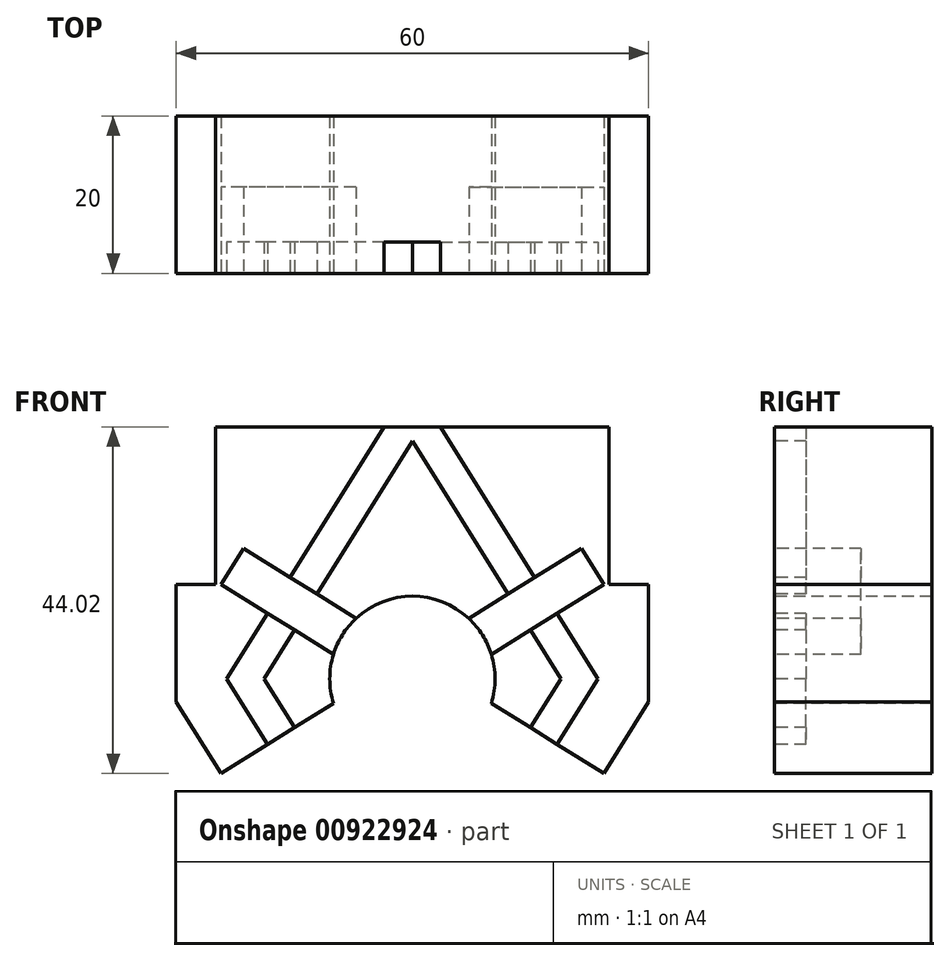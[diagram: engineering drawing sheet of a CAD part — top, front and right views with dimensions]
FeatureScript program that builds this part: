
annotation { "Feature Type Name" : "Feature", "Feature Type Description" : "" }
export const myFeature = defineFeature(function(context is Context, id is Id, definition is map)
    precondition{}
    {
        {
            var Q0;
            Q0=qCreatedBy(makeId("Front.planeOp"),FACE);
            var sketch = newSketch(context, id + "F0", { "sketchPlane" : qUnion([Q0])});
            skLineSegment(sketch, "E0", {"start": v(-28.13, -17.58) * mm, "end": v(31.4, 19.63) * mm, "construction": true});
            skLineSegment(sketch, "E1", {"start": v(7.3, 22.28) * mm, "end": v(22.97, -2.8) * mm, "construction": true});
            skArc(sketch, "E2", {"start": v(10.04, -3.09) * mm, "mid": v(0, 10.5) * mm, "end": v(-10.04, -3.09) * mm});
            skLineSegment(sketch, "E3", {"start": v(0, -23.09) * mm, "end": v(0, 36.36) * mm, "construction": true});
            skLineSegment(sketch, "E4", {"start": v(-33.15, 0) * mm, "end": v(34.43, 0) * mm, "construction": true});
            skLineSegment(sketch, "E5", {"start": v(0, 32) * mm, "end": v(25, 32) * mm});
            skLineSegment(sketch, "E6", {"start": v(25, 32) * mm, "end": v(25, 12) * mm});
            skLineSegment(sketch, "E7", {"start": v(25, 12) * mm, "end": v(30, 12) * mm});
            skLineSegment(sketch, "E8", {"start": v(30, 12) * mm, "end": v(30, -2.94) * mm});
            skLineSegment(sketch, "E9", {"start": v(30, -2.94) * mm, "end": v(24.33, -12.02) * mm});
            skLineSegment(sketch, "E10.MirrorCS", {"start": v(0, 32) * mm, "end": v(-25, 32) * mm});
            skLineSegment(sketch, "E11.MirrorCS", {"start": v(-25, 32) * mm, "end": v(-25, 12) * mm});
            skLineSegment(sketch, "E12.MirrorCS", {"start": v(-25, 12) * mm, "end": v(-30, 12) * mm});
            skLineSegment(sketch, "E13.MirrorCS", {"start": v(-30, 12) * mm, "end": v(-30, -2.94) * mm});
            skLineSegment(sketch, "E14.MirrorCS", {"start": v(-30, -2.94) * mm, "end": v(-24.33, -12.02) * mm});
            skLineSegment(sketch, "E15", {"start": v(7.17, 7.67) * mm, "end": v(21.47, 16.6) * mm});
            skLineSegment(sketch, "E16.MirrorCS", {"start": v(10.04, 3.09) * mm, "end": v(24.33, 12.02) * mm});
            skLineSegment(sketch, "E17", {"start": v(21.47, 16.6) * mm, "end": v(24.33, 12.02) * mm});
            skLineSegment(sketch, "E18", {"start": v(0, 30.2) * mm, "end": v(18.87, 0) * mm});
            skLineSegment(sketch, "E19", {"start": v(3.59, 32) * mm, "end": v(23.58, 0) * mm});
            skLineSegment(sketch, "E20.MirrorCS", {"start": v(0, 30.2) * mm, "end": v(-18.87, 0) * mm});
            skLineSegment(sketch, "E21.MirrorCS", {"start": v(-3.59, 32) * mm, "end": v(-23.58, 0) * mm});
            skLineSegment(sketch, "E22.MirrorCS", {"start": v(-7.17, 7.67) * mm, "end": v(-21.47, 16.6) * mm});
            skLineSegment(sketch, "E23.MirrorCS", {"start": v(-10.04, 3.09) * mm, "end": v(-24.33, 12.02) * mm});
            skLineSegment(sketch, "E24.MirrorCS", {"start": v(-21.47, 16.6) * mm, "end": v(-24.33, 12.02) * mm});
            skLineSegment(sketch, "E25.MirrorCS", {"start": v(-15, -6.19) * mm, "end": v(-18.87, 0) * mm});
            skLineSegment(sketch, "E26.MirrorCS", {"start": v(-18.4, -8.3) * mm, "end": v(-23.58, 0) * mm});
            skLineSegment(sketch, "E27.MirrorCS", {"start": v(18.4, -8.3) * mm, "end": v(23.58, 0) * mm});
            skLineSegment(sketch, "E28.MirrorCS", {"start": v(15, -6.19) * mm, "end": v(18.87, 0) * mm});
            skLineSegment(sketch, "E29.MirrorCS", {"start": v(10.04, -3.09) * mm, "end": v(24.33, -12.02) * mm});
            skLineSegment(sketch, "E30.MirrorCS", {"start": v(-10.04, -3.09) * mm, "end": v(-24.33, -12.02) * mm});
            skSolve(sketch);
        }
        {
            var Q0;
            Q0=qSketchRegion(id+"F0",true);
            var Q1;
            {var subQ1=sQuery(id+"F0.wireOp",EDGE,"E18");var subQ8=sQuery(id+"F0.wireOp",EDGE,"E15");var subQ10=makeQuery(id+"F0.imprint","INTERSECT",VERTEX,{"derivedFrom":[subQ8,subQ1]});Q1=makeQuery(id+"F0.imprint","IMPRINT",FACE,{"disambiguationData":[TD([[makeQuery(id+"F0.imprint","IMPRINT",EDGE,{"disambiguationData":[TD([[subQ10,-1.0]])],"derivedFrom":subQ8}),1.0]])]});}
            var Q2;
            {var subQ0=sQuery(id+"F0.wireOp",EDGE,"E17");Q2=makeQuery(id+"F0.imprint","IMPRINT",FACE,{"disambiguationData":[TD([[makeQuery(id+"F0.imprint","IMPRINT",EDGE,{"derivedFrom":subQ0}),-1.0]])]});}
            var Q3;
            {var subQ0=sQuery(id+"F0.wireOp",EDGE,"E18");var subQ1=sQuery(id+"F0.wireOp",EDGE,"E15");var subQ2=makeQuery(id+"F0.imprint","INTERSECT",VERTEX,{"derivedFrom":[subQ1,subQ0]});Q3=makeQuery(id+"F0.imprint","IMPRINT",FACE,{"disambiguationData":[TD([[makeQuery(id+"F0.imprint","IMPRINT",EDGE,{"disambiguationData":[TD([[subQ2,-1.0]])],"derivedFrom":subQ1}),-1.0]])]});}
            var Q4;
            {var subQ0=sQuery(id+"F0.wireOp",EDGE,"E22.MirrorCS");var subQ1=sQuery(id+"F0.wireOp",EDGE,"E20.MirrorCS");var subQ2=makeQuery(id+"F0.imprint","INTERSECT",VERTEX,{"derivedFrom":[subQ1,subQ0]});Q4=makeQuery(id+"F0.imprint","IMPRINT",FACE,{"disambiguationData":[TD([[makeQuery(id+"F0.imprint","IMPRINT",EDGE,{"disambiguationData":[TD([[subQ2,-1.0]])],"derivedFrom":subQ1}),-1.0]])]});}
            var Q5;
            {var subQ5=sQuery(id+"F0.wireOp",EDGE,"E24.MirrorCS");Q5=makeQuery(id+"F0.imprint","IMPRINT",FACE,{"disambiguationData":[TD([[makeQuery(id+"F0.imprint","IMPRINT",EDGE,{"derivedFrom":subQ5}),1.0]])]});}
            extrude(context, id + "F1", {"entities" : qUnion([Q0, Q1, Q2, Q3, Q4, Q5]), "oppositeDirection" : true, "depth" : 20 * mm, "offsetDistance" : 25 * mm});
        }
        {
            var Q0;
            {var subQ0=sQuery(id+"F0.wireOp",EDGE,"E17");Q0=makeQuery(id+"F0.imprint","IMPRINT",FACE,{"disambiguationData":[TD([[makeQuery(id+"F0.imprint","IMPRINT",EDGE,{"derivedFrom":subQ0}),-1.0]])]});}
            var Q1;
            {var subQ0=sQuery(id+"F0.wireOp",EDGE,"E18");var subQ1=sQuery(id+"F0.wireOp",EDGE,"E15");var subQ2=makeQuery(id+"F0.imprint","INTERSECT",VERTEX,{"derivedFrom":[subQ1,subQ0]});Q1=makeQuery(id+"F0.imprint","IMPRINT",FACE,{"disambiguationData":[TD([[makeQuery(id+"F0.imprint","IMPRINT",EDGE,{"disambiguationData":[TD([[subQ2,-1.0]])],"derivedFrom":subQ1}),-1.0]])]});}
            var Q2;
            {var subQ0=sQuery(id+"F0.wireOp",EDGE,"E15");var subQ1=sQuery(id+"F0.wireOp",EDGE,"E2");var subQ2=makeQuery(id+"F0.imprint","INTERSECT",VERTEX,{"derivedFrom":[subQ1,subQ0]});Q2=makeQuery(id+"F0.imprint","IMPRINT",FACE,{"disambiguationData":[TD([[makeQuery(id+"F0.imprint","IMPRINT",EDGE,{"disambiguationData":[TD([[subQ2,1.0]])],"derivedFrom":subQ1}),-1.0]])]});}
            var Q3;
            {var subQ0=sQuery(id+"F0.wireOp",EDGE,"E22.MirrorCS");var subQ1=sQuery(id+"F0.wireOp",EDGE,"E20.MirrorCS");var subQ2=makeQuery(id+"F0.imprint","INTERSECT",VERTEX,{"derivedFrom":[subQ1,subQ0]});Q3=makeQuery(id+"F0.imprint","IMPRINT",FACE,{"disambiguationData":[TD([[makeQuery(id+"F0.imprint","IMPRINT",EDGE,{"disambiguationData":[TD([[subQ2,-1.0]])],"derivedFrom":subQ1}),-1.0]])]});}
            var Q4;
            {var subQ0=sQuery(id+"F0.wireOp",EDGE,"E22.MirrorCS");var subQ1=sQuery(id+"F0.wireOp",EDGE,"E2");var subQ2=makeQuery(id+"F0.imprint","INTERSECT",VERTEX,{"derivedFrom":[subQ1,subQ0]});Q4=makeQuery(id+"F0.imprint","IMPRINT",FACE,{"disambiguationData":[TD([[makeQuery(id+"F0.imprint","IMPRINT",EDGE,{"disambiguationData":[TD([[subQ2,-1.0]])],"derivedFrom":subQ1}),-1.0]])]});}
            var Q5;
            {var subQ5=sQuery(id+"F0.wireOp",EDGE,"E24.MirrorCS");Q5=makeQuery(id+"F0.imprint","IMPRINT",FACE,{"disambiguationData":[TD([[makeQuery(id+"F0.imprint","IMPRINT",EDGE,{"derivedFrom":subQ5}),1.0]])]});}
            extrude(context, id + "F2", {"entities" : qUnion([Q0, Q1, Q2, Q3, Q4, Q5]), "operationType" : NewBodyOperationType.REMOVE, "oppositeDirection" : true, "depth" : 11 * mm, "offsetDistance" : 25 * mm});
        }
        {
            var Q0;
            {var subQ0=sQuery(id+"F0.wireOp",EDGE,"E25.MirrorCS");Q0=makeQuery(id+"F0.imprint","IMPRINT",FACE,{"disambiguationData":[TD([[makeQuery(id+"F0.imprint","IMPRINT",EDGE,{"derivedFrom":subQ0}),1.0]])]});}
            var Q1;
            {var subQ1=sQuery(id+"F0.wireOp",EDGE,"E18");var subQ8=sQuery(id+"F0.wireOp",EDGE,"E15");var subQ10=makeQuery(id+"F0.imprint","INTERSECT",VERTEX,{"derivedFrom":[subQ8,subQ1]});Q1=makeQuery(id+"F0.imprint","IMPRINT",FACE,{"disambiguationData":[TD([[makeQuery(id+"F0.imprint","IMPRINT",EDGE,{"disambiguationData":[TD([[subQ10,-1.0]])],"derivedFrom":subQ8}),1.0]])]});}
            var Q2;
            {var subQ0=sQuery(id+"F0.wireOp",EDGE,"E27.MirrorCS");Q2=makeQuery(id+"F0.imprint","IMPRINT",FACE,{"disambiguationData":[TD([[makeQuery(id+"F0.imprint","IMPRINT",EDGE,{"derivedFrom":subQ0}),1.0]])]});}
            extrude(context, id + "F3", {"entities" : qUnion([Q0, Q1, Q2]), "operationType" : NewBodyOperationType.REMOVE, "oppositeDirection" : true, "depth" : 4 * mm, "offsetDistance" : 25 * mm});
        }
    });
